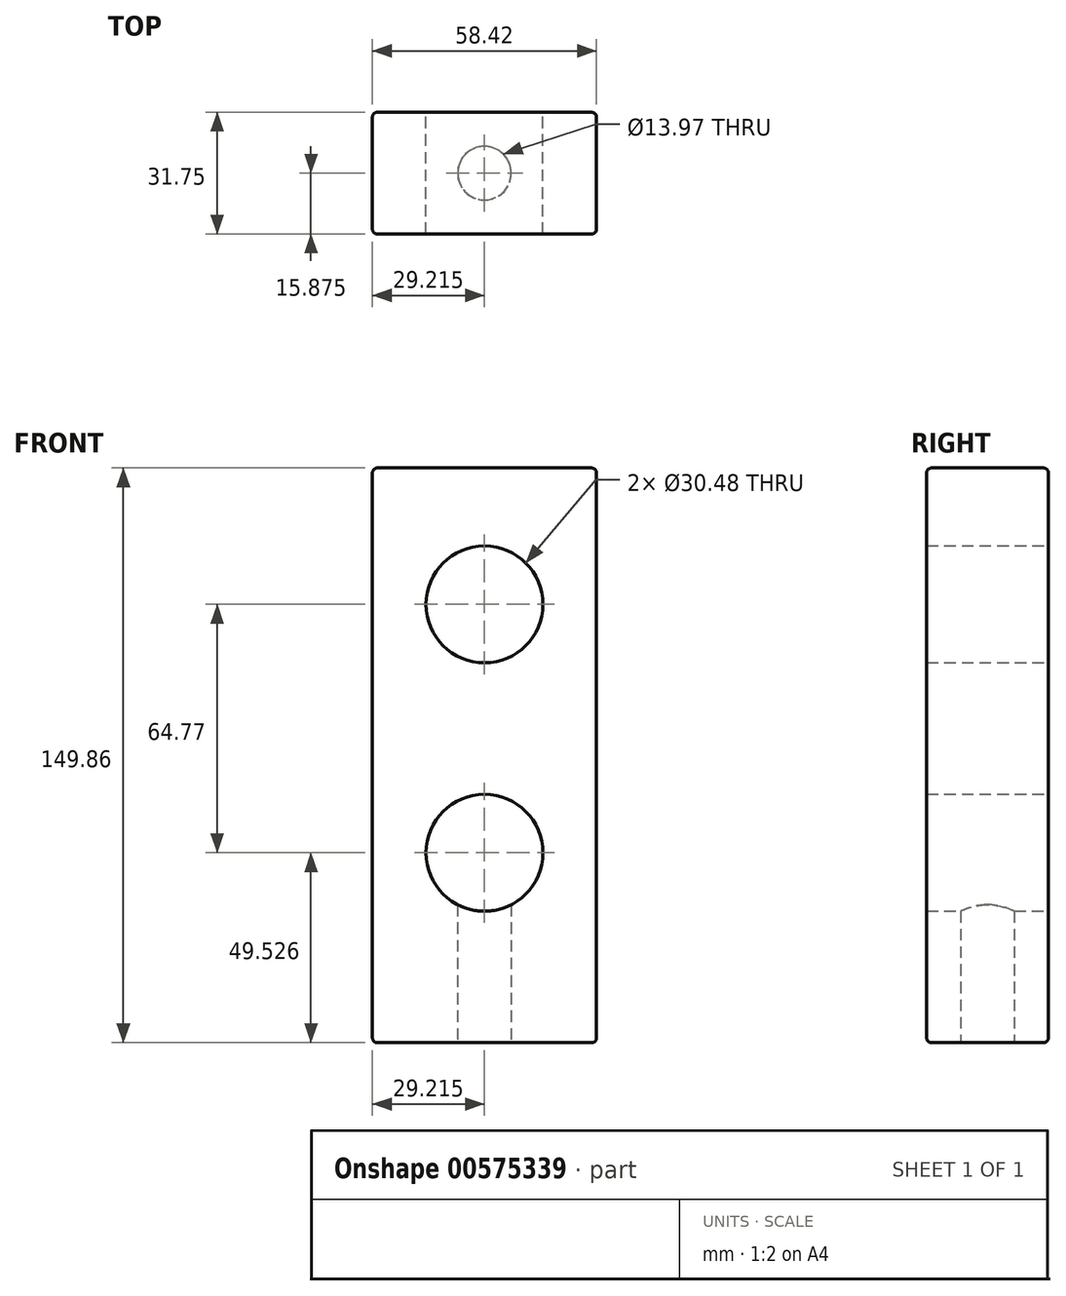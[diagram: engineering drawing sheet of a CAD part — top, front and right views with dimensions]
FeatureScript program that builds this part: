
annotation { "Feature Type Name" : "Feature", "Feature Type Description" : "" }
export const myFeature = defineFeature(function(context is Context, id is Id, definition is map)
    precondition{}
    {
        {
            var Q0;
            Q0=qCreatedBy(makeId("Front.planeOp"),FACE);
            var sketch = newSketch(context, id + "F0", { "sketchPlane" : qUnion([Q0])});
            skLineSegment(sketch, "E0", {"start": v(-48.49, -64.51) * mm, "end": v(-48.49, 85.35) * mm});
            skLineSegment(sketch, "E1", {"start": v(-48.49, 85.35) * mm, "end": v(9.93, 85.35) * mm});
            skLineSegment(sketch, "E2", {"start": v(-48.49, -64.51) * mm, "end": v(9.93, -64.51) * mm});
            skLineSegment(sketch, "E3", {"start": v(9.93, 85.35) * mm, "end": v(9.93, -64.51) * mm});
            skCircle(sketch, "E4", {"center": v(-19.28, 49.79) * mm, "radius": 15.24 * mm});
            skCircle(sketch, "E5", {"center": v(-19.28, -14.98) * mm, "radius": 15.24 * mm});
            skSolve(sketch);
        }
        {
            var Q0;
            Q0 = qSketchRegion(id + "F0", true);
            extrude(context, id + "F1", {"entities" : qUnion([Q0]), "depth" : 31.75 * mm, "offsetDistance" : 25.4 * mm});
        }
        {
            var Q0;
            Q0=makeQuery(id+"F1.opExtrude","SWEPT_FACE",FACE,{"disambiguationData":[OSD([sQuery(id+"F0.wireOp",EDGE,"E2")])]});
            var sketch = newSketch(context, id + "F2", { "sketchPlane" : qUnion([Q0])});
            skCircle(sketch, "E6", {"center": v(-19.28, 15.88) * mm, "radius": 6.99 * mm});
            skSolve(sketch);
        }
        {
            var Q0;
            Q0 = qSketchRegion(id + "F2", true);
            extrude(context, id + "F3", {"entities" : qUnion([Q0]), "operationType" : NewBodyOperationType.REMOVE, "oppositeDirection" : true, "depth" : 47 * mm, "offsetDistance" : 25.4 * mm});
        }
        {
            var Q0;
            Q0=makeQuery(id+"F1.opExtrude","CAP_EDGE",EDGE,{"disambiguationData":[OSD([sQuery(id+"F0.wireOp",EDGE,"E0")])],"isStart":false});
            var Q1;
            Q1=makeQuery(id+"F1.opExtrude","CAP_EDGE",EDGE,{"disambiguationData":[OSD([sQuery(id+"F0.wireOp",EDGE,"E3")])],"isStart":false});
            var Q2;
            Q2=makeQuery(id+"F1.opExtrude","CAP_EDGE",EDGE,{"disambiguationData":[OSD([sQuery(id+"F0.wireOp",EDGE,"E2")])],"isStart":false});
            var Q3;
            Q3=makeQuery(id+"F1.opExtrude","CAP_EDGE",EDGE,{"disambiguationData":[OSD([sQuery(id+"F0.wireOp",EDGE,"E1")])],"isStart":false});
            var Q4;
            Q4=makeQuery(id+"F1.opExtrude","SWEPT_EDGE",EDGE,{"disambiguationData":[OSD([sQuery(id+"F0.wireOp",EDGE,"E0"),sQuery(id+"F0.wireOp",EDGE,"E2")])]});
            var Q5;
            Q5=makeQuery(id+"F1.opExtrude","SWEPT_EDGE",EDGE,{"disambiguationData":[OSD([sQuery(id+"F0.wireOp",EDGE,"E2"),sQuery(id+"F0.wireOp",EDGE,"E3")])]});
            var Q6;
            Q6=makeQuery(id+"F1.opExtrude","CAP_EDGE",EDGE,{"disambiguationData":[OSD([sQuery(id+"F0.wireOp",EDGE,"E0")])],"isStart":true});
            var Q7;
            Q7=makeQuery(id+"F1.opExtrude","SWEPT_EDGE",EDGE,{"disambiguationData":[OSD([sQuery(id+"F0.wireOp",EDGE,"E1"),sQuery(id+"F0.wireOp",EDGE,"E3")])]});
            var Q8;
            Q8=makeQuery(id+"F1.opExtrude","CAP_EDGE",EDGE,{"disambiguationData":[OSD([sQuery(id+"F0.wireOp",EDGE,"E3")])],"isStart":true});
            var Q9;
            Q9=makeQuery(id+"F1.opExtrude","CAP_EDGE",EDGE,{"disambiguationData":[OSD([sQuery(id+"F0.wireOp",EDGE,"E2")])],"isStart":true});
            var Q10;
            Q10=makeQuery(id+"F1.opExtrude","CAP_EDGE",EDGE,{"disambiguationData":[OSD([sQuery(id+"F0.wireOp",EDGE,"E1")])],"isStart":true});
            var Q11;
            Q11=makeQuery(id+"F1.opExtrude","SWEPT_EDGE",EDGE,{"disambiguationData":[OSD([sQuery(id+"F0.wireOp",EDGE,"E0"),sQuery(id+"F0.wireOp",EDGE,"E1")])]});
            fillet(context, id + "F4", {"entities" : qUnion([Q0, Q1, Q2, Q3, Q4, Q5, Q6, Q7, Q8, Q9, Q10, Q11]), "radius" : 1.27 * mm, "tangentPropagation" : true, "allowEdgeOverflow" : false});
        }
    });
